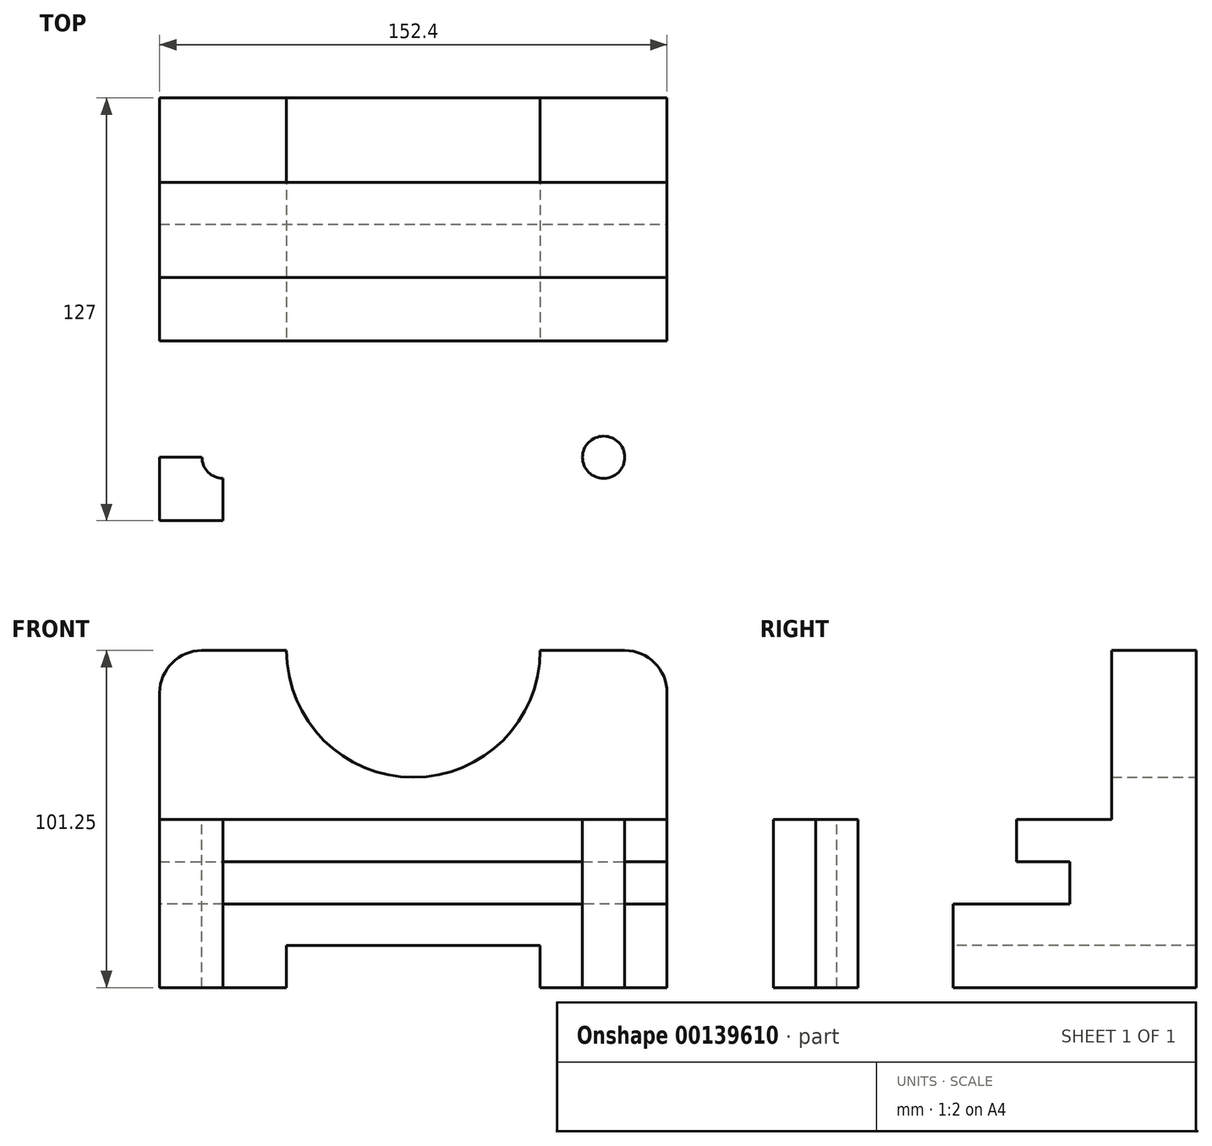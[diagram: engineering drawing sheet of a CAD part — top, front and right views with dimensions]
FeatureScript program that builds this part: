
annotation { "Feature Type Name" : "Feature", "Feature Type Description" : "" }
export const myFeature = defineFeature(function(context is Context, id is Id, definition is map)
    precondition{}
    {
        {
            var Q0;
            Q0=qCreatedBy(makeId("Front.planeOp"),FACE);
            var sketch = newSketch(context, id + "F0", { "sketchPlane" : qUnion([Q0])});
            skLineSegment(sketch, "E0", {"start": v(0, 0) * mm, "end": v(38.1, 0) * mm});
            skLineSegment(sketch, "E1", {"start": v(152.4, 0) * mm, "end": v(152.4, 50.45) * mm});
            skLineSegment(sketch, "E2", {"start": v(152.4, 50.45) * mm, "end": v(0, 50.45) * mm});
            skLineSegment(sketch, "E3", {"start": v(0, 50.45) * mm, "end": v(0, -0.35) * mm});
            skLineSegment(sketch, "E4", {"start": v(152.4, 0) * mm, "end": v(114.3, 0) * mm});
            skLineSegment(sketch, "E5", {"start": v(38.1, 0) * mm, "end": v(38.1, 12.7) * mm});
            skLineSegment(sketch, "E6", {"start": v(38.1, 12.7) * mm, "end": v(114.3, 12.7) * mm});
            skLineSegment(sketch, "E7", {"start": v(114.3, 12.7) * mm, "end": v(114.3, 0) * mm});
            skLineSegment(sketch, "E8.trimOffspring", {"start": v(114.3, 0) * mm, "end": v(152.4, 0) * mm});
            skSolve(sketch);
        }
        {
            var Q0;
            Q0 = qSketchRegion(id + "F0", true);
            extrude(context, id + "F1", {"entities" : qUnion([Q0]), "oppositeDirection" : true, "depth" : 127 * mm});
        }
        {
            var Q0;
            Q0=makeQuery(id+"F1.opExtrude","SWEPT_FACE",FACE,{"disambiguationData":[OSD([sQuery(id+"F0.wireOp",EDGE,"E1")])]});
            var sketch = newSketch(context, id + "F2", { "sketchPlane" : qUnion([Q0])});
            skLineSegment(sketch, "E9", {"start": v(0, 50.45) * mm, "end": v(53.97, 50.45) * mm});
            skLineSegment(sketch, "E10", {"start": v(53.97, 50.45) * mm, "end": v(53.97, 37.75) * mm});
            skLineSegment(sketch, "E11", {"start": v(53.97, 37.75) * mm, "end": v(38.23, 37.75) * mm});
            skLineSegment(sketch, "E12", {"start": v(53.97, 50.45) * mm, "end": v(73.03, 50.45) * mm});
            skLineSegment(sketch, "E13", {"start": v(73.03, 50.45) * mm, "end": v(73.03, 37.75) * mm});
            skLineSegment(sketch, "E14", {"start": v(38.23, 37.75) * mm, "end": v(38.23, 25.05) * mm});
            skLineSegment(sketch, "E15", {"start": v(38.23, 25.05) * mm, "end": v(89.03, 25.05) * mm});
            skLineSegment(sketch, "E16", {"start": v(73.03, 37.75) * mm, "end": v(89.03, 37.75) * mm});
            skLineSegment(sketch, "E17", {"start": v(89.03, 37.75) * mm, "end": v(89.03, 25.05) * mm});
            skSolve(sketch);
        }
        {
            var Q0;
            Q0 = qSketchRegion(id + "F2", true);
            extrude(context, id + "F3", {"entities" : qUnion([Q0]), "operationType" : NewBodyOperationType.REMOVE, "endBound" : BoundingType.UP_TO_NEXT, "oppositeDirection" : true, "depth" : 25.4 * mm});
        }
        {
            var Q0;
            {var subQ2=sQuery(id+"F0.wireOp",EDGE,"E2");Q0=makeQuery(id+"F3.boolean.opBoolean","SPLIT",FACE,{"disambiguationData":[TD([makeQuery(id+"F3.opExtrude","SWEPT_FACE",FACE,{"disambiguationData":[OSD([sQuery(id+"F2.wireOp",EDGE,"E13")])]})])],"derivedFrom":makeQuery(id+"F1.opExtrude","SWEPT_FACE",FACE,{"disambiguationData":[OSD([subQ2])]})});}
            var sketch = newSketch(context, id + "F4", { "sketchPlane" : qUnion([Q0])});
            skLineSegment(sketch, "E18", {"start": v(152.4, 127) * mm, "end": v(152.4, 101.6) * mm});
            skLineSegment(sketch, "E19", {"start": v(152.4, 101.6) * mm, "end": v(0, 101.6) * mm});
            skPoint(sketch, "E19.endSnap0", {"position": v(0, 100.01) * mm});
            skLineSegment(sketch, "E20", {"start": v(0, 101.6) * mm, "end": v(0, 127) * mm});
            skLineSegment(sketch, "E21", {"start": v(0, 127) * mm, "end": v(152.4, 127) * mm});
            skSolve(sketch);
        }
        {
            var Q0;
            Q0 = qSketchRegion(id + "F4", true);
            extrude(context, id + "F5", {"entities" : qUnion([Q0]), "operationType" : NewBodyOperationType.ADD, "depth" : 50.8 * mm});
        }
        {
            var Q0;
            Q0=makeQuery(id+"F5.boolean.opBoolean","MERGE",FACE,{"derivedFrom":[makeQuery(id+"F1.opExtrude","CAP_FACE",FACE,{"disambiguationData":[OSD([sQuery(id+"F0.wireOp",EDGE,"E1"),sQuery(id+"F0.wireOp",EDGE,"E2"),sQuery(id+"F0.wireOp",EDGE,"E3"),sQuery(id+"F0.wireOp",EDGE,"E0"),sQuery(id+"F0.wireOp",EDGE,"E5"),sQuery(id+"F0.wireOp",EDGE,"E6"),sQuery(id+"F0.wireOp",EDGE,"E7"),sQuery(id+"F0.wireOp",EDGE,"E8.trimOffspring")])],"isStart":false}),makeQuery(id+"F5.opExtrude","SWEPT_FACE",FACE,{"disambiguationData":[OSD([sQuery(id+"F4.wireOp",EDGE,"E21")])]})]});
            var sketch = newSketch(context, id + "F6", { "sketchPlane" : qUnion([Q0])});
            skSolve(sketch);
        }
        {
            var Q0;
            Q0=makeQuery(id+"F6.imprint","IMPRINT",FACE,{"disambiguationData":[TD([[makeQuery(id+"F6.imprint","IMPRINT",EDGE,{"derivedFrom":makeQuery(id+"F1.opExtrude","CAP_EDGE",EDGE,{"disambiguationData":[OSD([sQuery(id+"F0.wireOp",EDGE,"E0")])],"isStart":false})}),-1.0]])]});
            var sketch = newSketch(context, id + "F7", { "sketchPlane" : qUnion([Q0])});
            skPoint(sketch, "E22.0", {"position": v(-152.4, 101.25) * mm});
            skLineSegment(sketch, "E23", {"start": v(-152.4, 101.25) * mm, "end": v(-76.2, 101.25) * mm});
            skArc(sketch, "E24", {"start": v(-114.3, 101.25) * mm, "mid": v(-76.2, 63.15) * mm, "end": v(-38.1, 101.25) * mm});
            skLineSegment(sketch, "E25", {"start": v(-76.2, 101.25) * mm, "end": v(-38.1, 101.25) * mm});
            skSolve(sketch);
        }
        {
            var Q0;
            Q0 = qSketchRegion(id + "F7", true);
            extrude(context, id + "F8", {"entities" : qUnion([Q0]), "operationType" : NewBodyOperationType.REMOVE, "endBound" : BoundingType.UP_TO_NEXT, "oppositeDirection" : true, "depth" : 25.4 * mm});
        }
        {
            var Q0;
            Q0=makeQuery(id+"F5.opExtrude","CAP_EDGE",EDGE,{"disambiguationData":[OSD([sQuery(id+"F4.wireOp",EDGE,"E18")])],"isStart":false});
            var Q1;
            Q1=makeQuery(id+"F5.opExtrude","CAP_EDGE",EDGE,{"disambiguationData":[OSD([sQuery(id+"F4.wireOp",EDGE,"E20")])],"isStart":false});
            fillet(context, id + "F9", {"entities" : qUnion([Q0, Q1]), "radius" : 12.7 * mm, "tangentPropagation" : true, "allowEdgeOverflow" : false});
        }
        {
            var Q0;
            {var subQ2=sQuery(id+"F0.wireOp",EDGE,"E2");Q0=makeQuery(id+"F3.boolean.opBoolean","SPLIT",FACE,{"disambiguationData":[TD([makeQuery(id+"F3.opExtrude","SWEPT_FACE",FACE,{"disambiguationData":[OSD([sQuery(id+"F2.wireOp",EDGE,"E10")])]})])],"derivedFrom":makeQuery(id+"F1.opExtrude","SWEPT_FACE",FACE,{"disambiguationData":[OSD([subQ2])]})});}
            var sketch = newSketch(context, id + "F10", { "sketchPlane" : qUnion([Q0])});
            skLineSegment(sketch, "E26", {"start": v(0, 0) * mm, "end": v(19.05, 0) * mm});
            skLineSegment(sketch, "E27", {"start": v(0, 0) * mm, "end": v(0, 19.05) * mm});
            skLineSegment(sketch, "E28.0", {"start": v(152.4, 0) * mm, "end": v(0, 0) * mm});
            skLineSegment(sketch, "E29", {"start": v(76.2, 0) * mm, "end": v(76.2, 28.05) * mm});
            skLineSegment(sketch, "E30", {"start": v(19.05, 19.05) * mm, "end": v(0, 19.05) * mm});
            skLineSegment(sketch, "E31", {"start": v(19.05, 0) * mm, "end": v(19.05, 19.05) * mm});
            skCircle(sketch, "E32", {"center": v(19.05, 19.05) * mm, "radius": 6.35 * mm});
            skCircle(sketch, "E33.MirrorC", {"center": v(133.35, 19.05) * mm, "radius": 6.35 * mm});
            skSolve(sketch);
        }
        {
            var Q0;
            {var subQ0=sQuery(id+"F10.wireOp",EDGE,"E31");var subQ1=sQuery(id+"F10.wireOp",EDGE,"E30");var subQ2=makeQuery(id+"F10.imprint","INTERSECT",VERTEX,{"derivedFrom":[subQ1,subQ0]});Q0=makeQuery(id+"F10.imprint","IMPRINT",FACE,{"disambiguationData":[TD([[makeQuery(id+"F10.imprint","IMPRINT",EDGE,{"disambiguationData":[TD([[subQ2,-1.0]])],"derivedFrom":subQ1}),-1.0]])]});}
            var Q1;
            {var subQ0=sQuery(id+"F10.wireOp",EDGE,"E31");var subQ1=sQuery(id+"F10.wireOp",EDGE,"E30");var subQ2=makeQuery(id+"F10.imprint","INTERSECT",VERTEX,{"derivedFrom":[subQ1,subQ0]});Q1=makeQuery(id+"F10.imprint","IMPRINT",FACE,{"disambiguationData":[TD([[makeQuery(id+"F10.imprint","IMPRINT",EDGE,{"disambiguationData":[TD([[subQ2,-1.0]])],"derivedFrom":subQ1}),1.0]])]});}
            var Q2;
            Q2=makeQuery(id+"F10.imprint","IMPRINT",FACE,{"disambiguationData":[TD([[makeQuery(id+"F10.imprint","IMPRINT",EDGE,{"derivedFrom":sQuery(id+"F10.wireOp",EDGE,"E33.MirrorC")}),-1.0]])]});
            extrude(context, id + "F11", {"entities" : qUnion([Q0, Q1, Q2]), "operationType" : NewBodyOperationType.REMOVE, "endBound" : BoundingType.UP_TO_NEXT, "oppositeDirection" : true, "depth" : 25.4 * mm});
        }
    });
